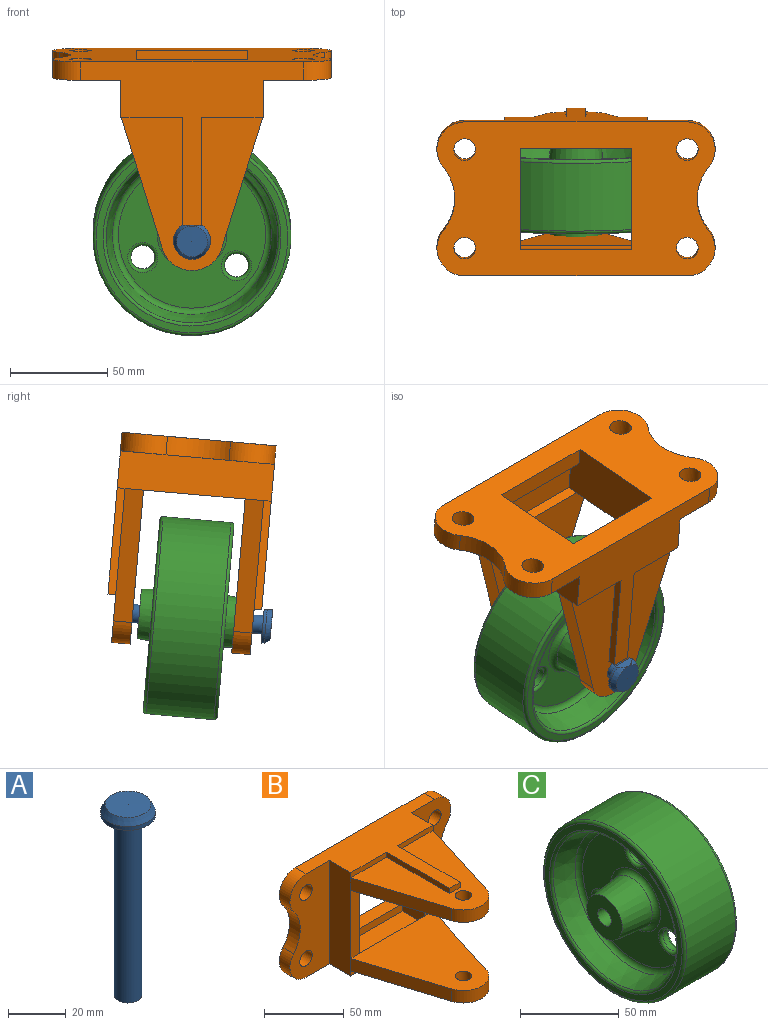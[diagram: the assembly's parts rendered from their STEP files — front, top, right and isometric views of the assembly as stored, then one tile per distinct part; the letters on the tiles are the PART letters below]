
ASSEMBLY  parts=3 mates=2
PART A: 7 faces, bbox 19.1x19.1x81 mm
  f0: cylinder r=9.53mm len=19.05mm, axis (0,0,-1), area 77.3mm2, adj f3,f4,f6
  f1: plane 9.53x9.53mm, normal (0,0,-1), area 71.3mm2, adj f2
  f2: cylinder r=4.76mm len=76.58mm, axis (0,0,-1), area 2291.4mm2, adj f1,f3
  f3: plane 19.05x17.46mm, normal (0,0,-1), area 202.4mm2, adj f0,f2,f6
  f4: cone r=9.53mm half-angle=29.7deg, axis (0,0,-1), area 151.5mm2, adj f0,f5,f6
  f5: cone r=0mm half-angle=89.7deg, axis (0,0,-1), area 198.6mm2, adj f4,f6
  f6: plane 10.56x4.37mm, normal (1,0,0), area 35.9mm2, adj f0,f3,f4,f5
PART B: 51 faces, bbox 142.9x108x79.4 mm
  f0: plane 142.88x79.38mm, normal (0,1,0), area 7268.5mm2, adj f16,f17,f18,f19,f20,f21,f22,f23
  f1: plane 57.15x5.61mm, normal (0,-1,0), area 320.8mm2, adj f29,f30,f31,f50
  f2: plane 79.38x73.03mm, normal (0,0,-1), area 3689.5mm2, adj f12,f13,f36,f45,f46,f47,f48
  f3: plane 79.38x73.03mm, normal (0,0,1), area 3157.3mm2, adj f8,f9,f38,f39,f40,f45,f46,f47
  f4: plane 79.38x73.03mm, normal (0,0,-1), area 3167.9mm2, adj f10,f11,f33,f34,f35,f41,f42,f43
  f5: plane 79.38x73.03mm, normal (0,0,1), area 3689.5mm2, adj f12,f13,f37,f41,f42,f43,f44
  f6: plane 79.38x19.05mm, normal (1,0,0), area 1512.1mm2, adj f9,f10,f12,f14,f17,f21,f43,f45
  f7: plane 79.38x19.05mm, normal (-1,0,0), area 1512.1mm2, adj f8,f11,f13,f15,f17,f21,f41,f47
  f8: plane 31.75x3.91mm, normal (0,-1,0), area 124.2mm2, adj f3,f7,f21,f39
  f9: plane 31.75x3.91mm, normal (0,-1,0), area 124.2mm2, adj f3,f6,f21,f38
  f10: plane 31.75x4.03mm, normal (0,-1,0), area 127.8mm2, adj f4,f6,f17,f34
  f11: plane 31.75x4.03mm, normal (0,-1,0), area 127.8mm2, adj f4,f7,f17,f33
  f12: plane 52.39x7.94mm, normal (0,-1,0), area 415.8mm2, adj f2,f5,f6,f29
  f13: plane 52.39x7.94mm, normal (0,-1,0), area 415.8mm2, adj f2,f5,f7,f31
  f14: plane 79.38x34.93mm, normal (0,-1,0), area 2233.1mm2, adj f6,f17,f18,f19,f20,f21,f23,f26
  f15: plane 79.38x34.93mm, normal (0,-1,0), area 2233.1mm2, adj f7,f16,f17,f21,f22,f24,f25,f27
  f16: cylinder r=14.29mm len=23.43mm, axis (0,1,0), area 308.3mm2, adj f0,f15,f17,f27
  f17: plane 114.3x83.34mm, normal (0,0,-1), area 3001.4mm2, adj f0,f6,f7,f10,f11,f14,f15,f16
  f18: cylinder r=14.29mm len=23.43mm, axis (0,1,0), area 308.3mm2, adj f0,f14,f17,f19
  f19: cylinder r=25.4mm len=32.51mm, axis (0,1,0), area 336mm2, adj f0,f14,f18,f20
  f20: cylinder r=14.29mm len=23.43mm, axis (0,1,0), area 308.3mm2, adj f0,f14,f19,f21
  f21: plane 114.3x84.46mm, normal (0,0,1), area 3012.1mm2, adj f0,f6,f7,f8,f9,f14,f15,f20
  f22: cylinder r=14.29mm len=23.43mm, axis (0,1,0), area 308.3mm2, adj f0,f15,f21,f27
  f23: cylinder r=5.56mm len=11.11mm, axis (0,1,0), area 332.5mm2, adj f0,f14
  f24: cylinder r=5.56mm len=11.11mm, axis (0,1,0), area 332.5mm2, adj f0,f15
  f25: cylinder r=5.56mm len=11.11mm, axis (0,1,0), area 332.5mm2, adj f0,f15
  f26: cylinder r=5.56mm len=11.11mm, axis (0,1,0), area 332.5mm2, adj f0,f14
  f27: cylinder r=25.4mm len=32.51mm, axis (0,1,0), area 336mm2, adj f0,f15,f16,f22
  f28: plane 57.15x19.05mm, normal (0,0,-1), area 1088.7mm2, adj f29,f31,f32,f36
  f29: plane 63.5x28.58mm, normal (-1,0,0), area 1708.7mm2, adj f0,f1,f12,f28,f30,f32,f36,f37
  f30: plane 57.15x19.05mm, normal (0,0,1), area 1088.7mm2, adj f1,f29,f31,f37
  f31: plane 63.5x28.58mm, normal (1,0,0), area 1708.7mm2, adj f0,f1,f13,f28,f30,f32,f36,f37
  f32: plane 57.15x5.5mm, normal (0,-1,0), area 314.3mm2, adj f28,f29,f31,f49
  f33: plane 54.76x4.03mm, normal (-1,0,0), area 220.5mm2, adj f4,f11,f17,f35
  f34: plane 54.76x4.03mm, normal (1,0,0), area 220.5mm2, adj f4,f10,f17,f35
  f35: plane 9.53x4.03mm, normal (0,-1,0), area 38.3mm2, adj f4,f17,f33,f34
  f36: plane 57.15x5.5mm, normal (0,1,0), area 314.3mm2, adj f2,f28,f29,f31
  f37: plane 57.15x5.61mm, normal (0,1,0), area 320.8mm2, adj f5,f29,f30,f31
  f38: plane 55.88x3.91mm, normal (1,0,0), area 218.6mm2, adj f3,f9,f21,f40
  f39: plane 55.88x3.91mm, normal (-1,0,0), area 218.6mm2, adj f3,f8,f21,f40
  f40: plane 9.53x3.91mm, normal (0,-1,0), area 37.3mm2, adj f3,f21,f38,f39
  f41: plane 68.24x21.36mm, normal (-0.95,-0.3,0), area 681.1mm2, adj f4,f5,f7,f42
  f42: cylinder r=15.88mm len=30.3mm, axis (0,0,-1), area 383.3mm2, adj f4,f5,f41,f43
  f43: plane 68.24x21.36mm, normal (0.95,-0.3,0), area 681.1mm2, adj f4,f5,f6,f42
  f44: cylinder r=5.16mm len=10.32mm, axis (0,0,-1), area 308.8mm2, adj f4,f5
  f45: plane 68.24x21.36mm, normal (0.95,-0.3,0), area 681.1mm2, adj f2,f3,f6,f46
  f46: cylinder r=15.88mm len=30.3mm, axis (0,0,1), area 383.3mm2, adj f2,f3,f45,f47
  f47: plane 68.24x21.36mm, normal (-0.95,-0.3,0), area 681.1mm2, adj f2,f3,f7,f46
  f48: cylinder r=5.16mm len=10.32mm, axis (0,0,1), area 308.8mm2, adj f2,f3
  f49: plane 57.15x9.53mm, normal (0,0,-1), area 544.4mm2, adj f0,f29,f31,f32
  f50: plane 57.15x9.53mm, normal (0,0,1), area 544.4mm2, adj f0,f1,f29,f31
PART C: 29 faces, bbox 50.8x110x110 mm
  f0: cylinder r=4.83mm len=50.8mm, axis (-1,0,0), area 1540.4mm2, adj f1,f17
  f1: plane 25.4x25.4mm, normal (1,0,0), area 433.5mm2, adj f0,f2
  f2: cone r=14.72mm half-angle=6deg, axis (-1,0,0), area 1678.4mm2, adj f1,f3
  f3: torus R=17.88mm, axis (-1,0,0), area 466.4mm2, adj f2,f4
  f4: plane 75.69x75.69mm, normal (1,0,0), area 2931.1mm2, adj f3,f5,f23,f24,f25
  f5: torus R=37.85mm, axis (-1,0,0), area 1040mm2, adj f4,f6
  f6: cone r=44.14mm half-angle=14.7deg, axis (1,0,0), area 3402.3mm2, adj f5,f7
  f7: torus R=45.68mm, axis (-1,0,0), area 587.2mm2, adj f6,f8
  f8: plane 98.43x98.43mm, normal (1,0,0), area 1054.3mm2, adj f7,f22
  f9: cylinder r=50.8mm len=101.6mm, axis (-1,0,0), area 11147.6mm2, adj f21,f22
  f10: plane 98.43x98.43mm, normal (-1,0,0), area 1054.3mm2, adj f11,f21
  f11: torus R=45.68mm, axis (-1,0,0), area 587.2mm2, adj f10,f12
  f12: cone r=44.14mm half-angle=14.7deg, axis (-1,0,0), area 3402.3mm2, adj f11,f13
  f13: torus R=37.85mm, axis (-1,0,0), area 1040mm2, adj f12,f14
  f14: plane 75.69x75.69mm, normal (-1,0,0), area 2931.1mm2, adj f13,f15,f26,f27,f28
  f15: torus R=17.88mm, axis (-1,0,0), area 466.4mm2, adj f14,f16
  f16: cone r=14.72mm half-angle=6deg, axis (1,0,0), area 1678.4mm2, adj f15,f17
  f17: plane 25.4x25.4mm, normal (-1,0,0), area 433.5mm2, adj f0,f16
  f18: cylinder r=6.15mm len=12.3mm, axis (-1,0,0), area 122.7mm2, adj f25,f26
  f19: cylinder r=6.15mm len=12.3mm, axis (-1,0,0), area 122.7mm2, adj f24,f27
  f20: cylinder r=6.15mm len=12.3mm, axis (-1,0,0), area 122.7mm2, adj f23,f28
  f21: torus R=49.21mm, axis (1,0,0), area 786.9mm2, adj f9,f10
  f22: torus R=49.21mm, axis (1,0,0), area 786.9mm2, adj f8,f9
  f23: torus R=7.74mm, axis (-1,0,0), area 105.4mm2, adj f4,f20
  f24: torus R=7.74mm, axis (-1,0,0), area 105.4mm2, adj f4,f19
  f25: torus R=7.74mm, axis (-1,0,0), area 105.4mm2, adj f4,f18
  f26: torus R=7.74mm, axis (-1,0,0), area 105.4mm2, adj f14,f18
  f27: torus R=7.74mm, axis (-1,0,0), area 105.4mm2, adj f14,f19
  f28: torus R=7.74mm, axis (-1,0,0), area 105.4mm2, adj f14,f20
PLACE A rot(axis=(0.59,-0.59,0.54),122.9deg) t=(-170.38,-38.05,-54.6)mm
PLACE B rot(axis=(1,0,0),95deg) t=(-169.55,-121.14,30.56)mm fixed
PLACE C rot(axis=(0,0.09,-1),90deg) t=(-169.55,-74.15,-48.24)mm
MATE revolute A.f0 <-> C.f0  axis (0,1,0.09) through (-170.38,-76.19,-57.94)mm
MATE slider A.f0 <-> B.f42  axis (0,1,0.09) through (-170.38,-38.05,-54.6)mm
